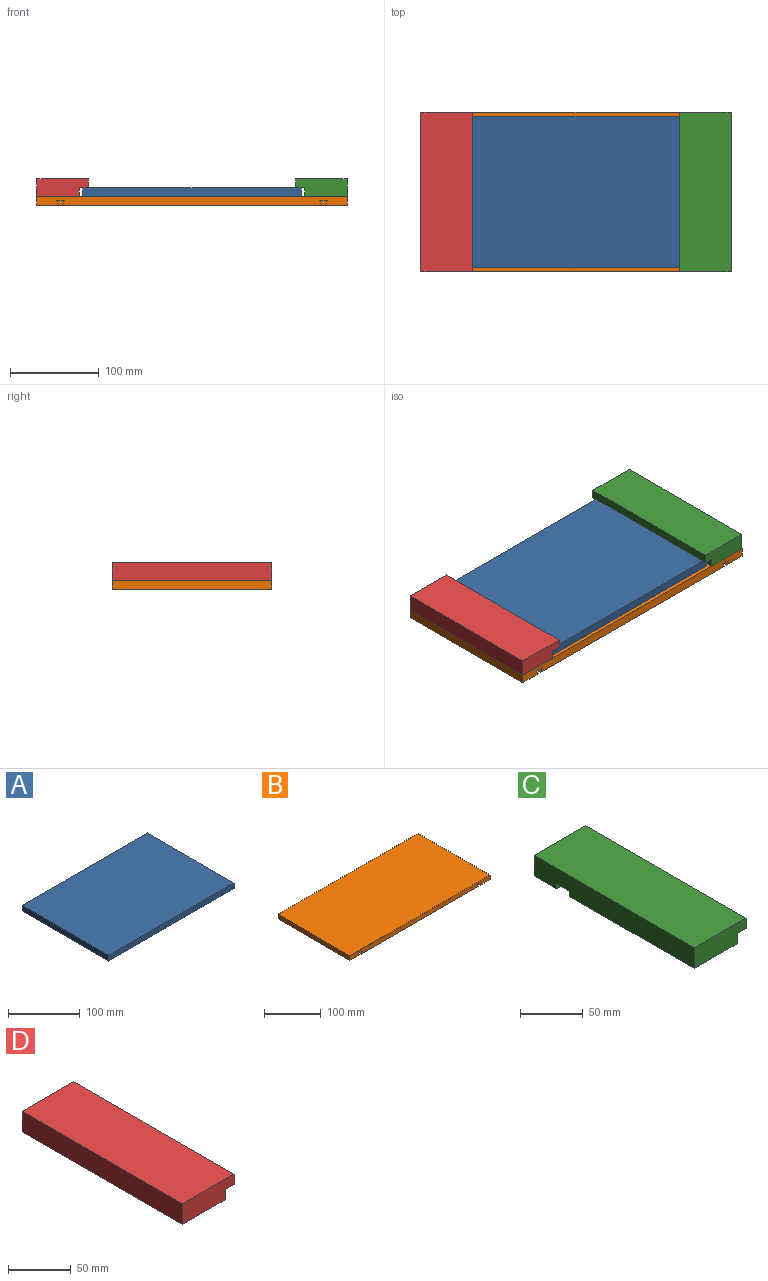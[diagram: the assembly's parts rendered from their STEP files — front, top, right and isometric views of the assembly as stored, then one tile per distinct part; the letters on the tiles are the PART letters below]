
ASSEMBLY  parts=4 mates=3
PART A: 6 faces, bbox 246.9x170.9x9.7 mm
  f0: plane 246.9x9.65mm, normal (0,-1,0), area 2382.6mm2, adj f1,f3,f4,f5
  f1: plane 170.9x9.65mm, normal (1,0,0), area 1649.2mm2, adj f0,f2,f4,f5
  f2: plane 246.9x9.65mm, normal (0,1,0), area 2382.6mm2, adj f1,f3,f4,f5
  f3: plane 170.9x9.65mm, normal (-1,0,0), area 1649.2mm2, adj f0,f2,f4,f5
  f4: plane 246.9x170.9mm, normal (0,0,1), area 42195.2mm2, adj f0,f1,f2,f3
  f5: plane 246.9x170.9mm, normal (0,0,-1), area 42195.2mm2, adj f0,f1,f2,f3
PART B: 14 faces, bbox 350x180x10 mm
  f0: plane 350x10mm, normal (0,-1,0), area 3440mm2, adj f1,f3,f4,f5,f6,f7,f8,f10
  f1: plane 180x10mm, normal (1,0,0), area 1800mm2, adj f0,f2,f4,f5
  f2: plane 350x10mm, normal (0,1,0), area 3500mm2, adj f1,f3,f4,f5
  f3: plane 180x10mm, normal (-1,0,0), area 1800mm2, adj f0,f2,f4,f5
  f4: plane 350x180mm, normal (0,0,1), area 63000mm2, adj f0,f1,f2,f3
  f5: plane 350x180mm, normal (0,0,-1), area 62100mm2, adj f0,f1,f2,f3,f7,f8,f9,f10
  f6: plane 150x9mm, normal (0,0,-1), area 1350mm2, adj f0,f7,f8,f9
  f7: plane 150x5mm, normal (0.86,0,0.51), area 874.6mm2, adj f0,f5,f6,f9
  f8: plane 150x5mm, normal (-0.86,0,0.51), area 874.6mm2, adj f0,f5,f6,f9
  f9: plane 9x5mm, normal (0,-1,0), area 30mm2, adj f5,f6,f7,f8
  f10: plane 150x5mm, normal (-0.86,0,0.51), area 874.6mm2, adj f0,f5,f11,f13
  f11: plane 150x9mm, normal (0,0,-1), area 1350mm2, adj f0,f10,f12,f13
  f12: plane 150x5mm, normal (0.86,0,0.51), area 874.6mm2, adj f0,f5,f11,f13
  f13: plane 9x5mm, normal (0,-1,0), area 30mm2, adj f5,f10,f11,f12
PART C: 12 faces, bbox 58x180x20 mm
  f0: plane 48x25mm, normal (0,0,-1), area 1200mm2, adj f1,f2,f4,f9
  f1: plane 58x20mm, normal (0,1,0), area 1060mm2, adj f0,f2,f4,f5,f7,f8
  f2: plane 180x20mm, normal (-1,0,0), area 3525mm2, adj f0,f1,f3,f5,f6,f9,f10,f11
  f3: plane 58x20mm, normal (0,-1,0), area 1060mm2, adj f2,f4,f5,f6,f7,f8
  f4: plane 180x10mm, normal (1,0,0), area 1725mm2, adj f0,f1,f3,f6,f7,f9,f10,f11
  f5: plane 180x58mm, normal (0,0,1), area 10440mm2, adj f1,f2,f3,f8
  f6: plane 140x48mm, normal (0,0,-1), area 6720mm2, adj f2,f3,f4,f10
  f7: plane 180x10mm, normal (0,0,-1), area 1800mm2, adj f1,f3,f4,f8
  f8: plane 180x10mm, normal (1,0,0), area 1800mm2, adj f1,f3,f5,f7
  f9: plane 48x5mm, normal (0,-1,0), area 240mm2, adj f0,f2,f4,f11
  f10: plane 48x5mm, normal (0,1,0), area 240mm2, adj f2,f4,f6,f11
  f11: plane 48x15mm, normal (0,0,-1), area 720mm2, adj f2,f4,f9,f10
PART D: 8 faces, bbox 58x180x20 mm
  f0: plane 58x20mm, normal (0,1,0), area 1060mm2, adj f1,f3,f4,f5,f6,f7
  f1: plane 180x20mm, normal (-1,0,0), area 3600mm2, adj f0,f2,f4,f5
  f2: plane 58x20mm, normal (0,-1,0), area 1060mm2, adj f1,f3,f4,f5,f6,f7
  f3: plane 180x10mm, normal (1,0,0), area 1800mm2, adj f0,f2,f5,f6
  f4: plane 180x58mm, normal (0,0,1), area 10440mm2, adj f0,f1,f2,f7
  f5: plane 180x48mm, normal (0,0,-1), area 8640mm2, adj f0,f1,f2,f3
  f6: plane 180x10mm, normal (0,0,-1), area 1800mm2, adj f0,f2,f3,f7
  f7: plane 180x10mm, normal (1,0,0), area 1800mm2, adj f0,f2,f4,f6
PLACE A t=(124,-85.24,4.85)mm
PLACE B t=(0.55,0.21,-5.15)mm
PLACE C rot(axis=(0,0,1),180deg) t=(151.55,0.21,4.85)mm
PLACE D t=(-150.45,0.21,4.85)mm
MATE revolute C.f3 <-> B.f2  axis (0,1,0) through (175.55,90.21,4.85)mm
MATE parallel D.f2 <-> B.f0  axis (0,-1,0) through (-174.45,-89.79,4.85)mm
MATE parallel A.f5 <-> B.f4  axis (0,0,-1) through (0.55,0.21,4.85)mm
